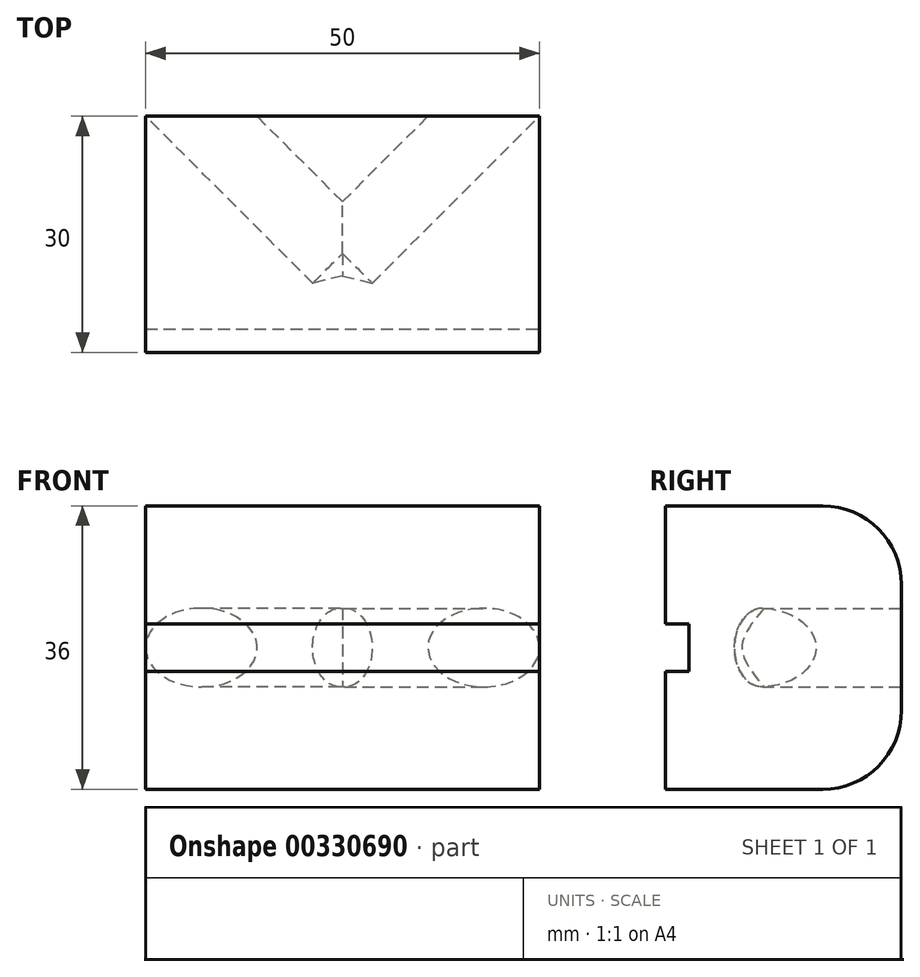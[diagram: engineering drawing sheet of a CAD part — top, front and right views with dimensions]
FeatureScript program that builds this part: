
annotation { "Feature Type Name" : "Feature", "Feature Type Description" : "" }
export const myFeature = defineFeature(function(context is Context, id is Id, definition is map)
    precondition{}
    {
        {
            var Q0;
            Q0=qCreatedBy(makeId("Front.planeOp"),FACE);
            var sketch = newSketch(context, id + "F0", { "sketchPlane" : qUnion([Q0])});
            skLineSegment(sketch, "E0.bottom", {"start": v(25, 18) * mm, "end": v(-25, 18) * mm});
            skLineSegment(sketch, "E0.top", {"start": v(25, -18) * mm, "end": v(-25, -18) * mm});
            skLineSegment(sketch, "E0.left", {"start": v(25, 18) * mm, "end": v(25, -18) * mm});
            skLineSegment(sketch, "E0.right", {"start": v(-25, 18) * mm, "end": v(-25, -18) * mm});
            skPoint(sketch, "E0.middle", {"position": v(0, 0) * mm});
            skSolve(sketch);
        }
        {
            var Q0;
            Q0=makeQuery(id+"F0.imprint","IMPRINT",FACE,{"disambiguationData":[TD([[makeQuery(id+"F0.imprint","IMPRINT",EDGE,{"derivedFrom":sQuery(id+"F0.wireOp",EDGE,"E0.bottom")}),1.0]])]});
            extrude(context, id + "F1", {"entities" : qUnion([Q0]), "depth" : 30 * mm});
        }
        {
            var Q0;
            Q0=makeQuery(id+"F1.opExtrude","CAP_EDGE",EDGE,{"disambiguationData":[OSD([sQuery(id+"F0.wireOp",EDGE,"E0.right")])],"isStart":true});
            cPlane(context, id + "F2", {"entities" : qUnion([Q0]), "cplaneType" : CPlaneType.LINE_ANGLE, "offset" : 25 * mm, "angle" : 45 * degree, "width" : 150 * mm, "height" : 150 * mm});
        }
        {
            var Q0;
            Q0=qCreatedBy(id+"F2.planeOp",FACE);
            var sketch = newSketch(context, id + "F3", { "sketchPlane" : qUnion([Q0])});
            skPoint(sketch, "E1", {"position": v(12.68, 0) * mm});
            skSolve(sketch);
        }
        {
            var Q0;
            Q0=sQuery(id+"F3.wireOp",VERTEX,"E1");
            var Q1;
            Q1=makeQuery(id+"F1.opExtrude","SWEPT_BODY",BODY,{"disambiguationData":[OSD([sQuery(id+"F0.wireOp",EDGE,"E0.bottom"),sQuery(id+"F0.wireOp",EDGE,"E0.top"),sQuery(id+"F0.wireOp",EDGE,"E0.left"),sQuery(id+"F0.wireOp",EDGE,"E0.right")])]});
            hole(context, id + "F4", {"style" : HoleStyle.SIMPLE, "endStyle" : HoleEndStyle.BLIND, "holeDiameter" : 10 * mm, "holeDepth" : 20 * mm, "tappedDepth" : 12 * mm, "tapClearance" : 3, "locations" : qUnion([Q0]), "scope" : qUnion([Q1])});
        }
        {
            var Q0;
            Q0=makeQuery(id+"F1.opExtrude","CAP_EDGE",EDGE,{"disambiguationData":[OSD([sQuery(id+"F0.wireOp",EDGE,"E0.left")])],"isStart":true});
            cPlane(context, id + "F5", {"entities" : qUnion([Q0]), "cplaneType" : CPlaneType.LINE_ANGLE, "offset" : 25 * mm, "angle" : 135 * degree, "width" : 150 * mm, "height" : 150 * mm});
        }
        {
            var Q0;
            Q0=qCreatedBy(id+"F5.planeOp",FACE);
            var sketch = newSketch(context, id + "F6", { "sketchPlane" : qUnion([Q0])});
            skPoint(sketch, "E2", {"position": v(-12.68, 0) * mm});
            skSolve(sketch);
        }
        {
            var Q0;
            Q0=sQuery(id+"F6.wireOp",VERTEX,"E2");
            var Q1;
            Q1=makeQuery(id+"F1.opExtrude","SWEPT_BODY",BODY,{"disambiguationData":[OSD([sQuery(id+"F0.wireOp",EDGE,"E0.bottom"),sQuery(id+"F0.wireOp",EDGE,"E0.top"),sQuery(id+"F0.wireOp",EDGE,"E0.left"),sQuery(id+"F0.wireOp",EDGE,"E0.right")])]});
            hole(context, id + "F7", {"style" : HoleStyle.SIMPLE, "endStyle" : HoleEndStyle.BLIND, "holeDiameter" : 10 * mm, "holeDepth" : 20 * mm, "tappedDepth" : 12 * mm, "tapClearance" : 3, "locations" : qUnion([Q0]), "scope" : qUnion([Q1])});
        }
        {
            var Q0;
            Q0=makeQuery(id+"F1.opExtrude","CAP_FACE",FACE,{"disambiguationData":[OSD([sQuery(id+"F0.wireOp",EDGE,"E0.bottom"),sQuery(id+"F0.wireOp",EDGE,"E0.top"),sQuery(id+"F0.wireOp",EDGE,"E0.left"),sQuery(id+"F0.wireOp",EDGE,"E0.right")])],"isStart":false});
            var sketch = newSketch(context, id + "F8", { "sketchPlane" : qUnion([Q0])});
            skLineSegment(sketch, "E3.bottom", {"start": v(-25, -3) * mm, "end": v(25, -3) * mm});
            skLineSegment(sketch, "E3.top", {"start": v(-25, 3) * mm, "end": v(25, 3) * mm});
            skLineSegment(sketch, "E3.left", {"start": v(-25, -3) * mm, "end": v(-25, 3) * mm});
            skLineSegment(sketch, "E3.right", {"start": v(25, -3) * mm, "end": v(25, 3) * mm});
            skSolve(sketch);
        }
        {
            var Q0;
            Q0=makeQuery(id+"F8.imprint","IMPRINT",FACE,{"disambiguationData":[TD([[makeQuery(id+"F8.imprint","IMPRINT",EDGE,{"derivedFrom":sQuery(id+"F8.wireOp",EDGE,"E3.bottom")}),1.0]])]});
            extrude(context, id + "F9", {"entities" : qUnion([Q0]), "operationType" : NewBodyOperationType.REMOVE, "oppositeDirection" : true, "depth" : 3 * mm});
        }
        {
            var Q0;
            Q0=makeQuery(id+"F1.opExtrude","CAP_EDGE",EDGE,{"disambiguationData":[OSD([sQuery(id+"F0.wireOp",EDGE,"E0.top")])],"isStart":true});
            var Q1;
            Q1=makeQuery(id+"F1.opExtrude","CAP_EDGE",EDGE,{"disambiguationData":[OSD([sQuery(id+"F0.wireOp",EDGE,"E0.bottom")])],"isStart":true});
            fillet(context, id + "F10", {"entities" : qUnion([Q0, Q1]), "radius" : 10 * mm, "tangentPropagation" : true, "allowEdgeOverflow" : false});
        }
    });
